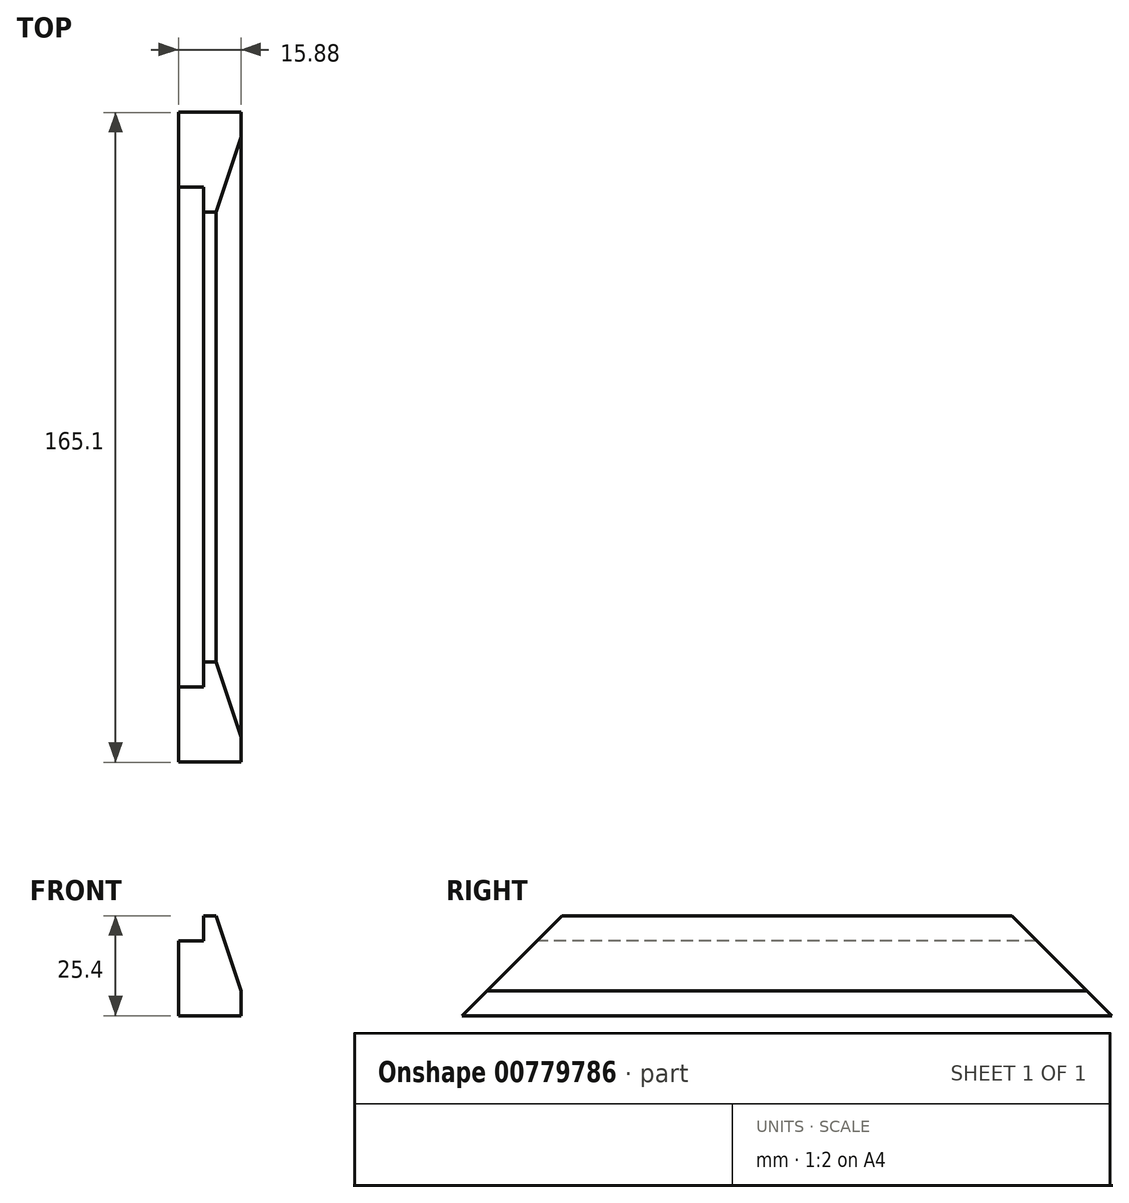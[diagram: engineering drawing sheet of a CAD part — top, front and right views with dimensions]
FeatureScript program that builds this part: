
annotation { "Feature Type Name" : "Feature", "Feature Type Description" : "" }
export const myFeature = defineFeature(function(context is Context, id is Id, definition is map)
    precondition{}
    {
        {
            var Q0;
            Q0=qCreatedBy(makeId("Right.planeOp"),FACE);
            var sketch = newSketch(context, id + "F0", { "sketchPlane" : qUnion([Q0])});
            skLineSegment(sketch, "E0.bottom", {"start": v(84.71, 12.7) * mm, "end": v(-80.39, 12.7) * mm});
            skLineSegment(sketch, "E0.top", {"start": v(84.71, -12.7) * mm, "end": v(-80.39, -12.7) * mm});
            skLineSegment(sketch, "E0.left", {"start": v(84.71, 12.7) * mm, "end": v(84.71, -12.7) * mm});
            skLineSegment(sketch, "E0.right", {"start": v(-80.39, 12.7) * mm, "end": v(-80.39, -12.7) * mm});
            skPoint(sketch, "E0.middle", {"position": v(2.16, 0) * mm});
            skSolve(sketch);
        }
        {
            var Q0;
            Q0 = qSketchRegion(id + "F0", true);
            extrude(context, id + "F1", {"entities" : qUnion([Q0]), "depth" : 15.88 * mm, "offsetDistance" : 25.4 * mm});
        }
        {
            var Q0;
            Q0=makeQuery(id+"F1.opExtrude","CAP_FACE",FACE,{"disambiguationData":[OSD([sQuery(id+"F0.wireOp",EDGE,"E0.bottom"),sQuery(id+"F0.wireOp",EDGE,"E0.top"),sQuery(id+"F0.wireOp",EDGE,"E0.left"),sQuery(id+"F0.wireOp",EDGE,"E0.right")])],"isStart":false});
            var sketch = newSketch(context, id + "F2", { "sketchPlane" : qUnion([Q0])});
            skLineSegment(sketch, "E1", {"start": v(-80.39, -12.7) * mm, "end": v(-54.99, 12.7) * mm});
            skLineSegment(sketch, "E2", {"start": v(84.71, -12.7) * mm, "end": v(59.31, 12.7) * mm});
            skSolve(sketch);
        }
        {
            var Q0;
            Q0=makeQuery(id+"F1.opExtrude","SWEPT_FACE",FACE,{"disambiguationData":[OSD([sQuery(id+"F0.wireOp",EDGE,"E0.right")])]});
            var sketch = newSketch(context, id + "F3", { "sketchPlane" : qUnion([Q0])});
            skLineSegment(sketch, "E3.bottom", {"start": v(0, 12.7) * mm, "end": v(6.35, 12.7) * mm});
            skLineSegment(sketch, "E3.top", {"start": v(0, 6.35) * mm, "end": v(6.35, 6.35) * mm});
            skLineSegment(sketch, "E3.left", {"start": v(0, 12.7) * mm, "end": v(0, 6.35) * mm});
            skLineSegment(sketch, "E3.right", {"start": v(6.35, 12.7) * mm, "end": v(6.35, 6.35) * mm});
            skSolve(sketch);
        }
        {
            var Q0;
            Q0 = qSketchRegion(id + "F3", true);
            extrude(context, id + "F4", {"entities" : qUnion([Q0]), "operationType" : NewBodyOperationType.REMOVE, "endBound" : BoundingType.THROUGH_ALL, "oppositeDirection" : true, "depth" : 25.4 * mm, "offsetDistance" : 25.4 * mm});
        }
        {
            var Q0;
            {var subQ0=sQuery(id+"F2.wireOp",EDGE,"E1");Q0=makeQuery(id+"F2.imprint","IMPRINT",FACE,{"disambiguationData":[TD([[makeQuery(id+"F2.imprint","IMPRINT",EDGE,{"derivedFrom":subQ0}),1.0]])]});}
            var Q1;
            {var subQ0=sQuery(id+"F2.wireOp",EDGE,"E2");Q1=makeQuery(id+"F2.imprint","IMPRINT",FACE,{"disambiguationData":[TD([[makeQuery(id+"F2.imprint","IMPRINT",EDGE,{"derivedFrom":subQ0}),-1.0]])]});}
            extrude(context, id + "F5", {"entities" : qUnion([Q0, Q1]), "operationType" : NewBodyOperationType.REMOVE, "endBound" : BoundingType.THROUGH_ALL, "oppositeDirection" : true, "depth" : 25.4 * mm, "offsetDistance" : 25.4 * mm});
        }
        {
            var Q0;
            Q0=makeQuery(id+"F1.opExtrude","CAP_EDGE",EDGE,{"disambiguationData":[OSD([sQuery(id+"F0.wireOp",EDGE,"E0.bottom")])],"isStart":false});
            chamfer(context, id + "F6", {"entities" : qUnion([Q0]), "chamferType" : ChamferType.OFFSET_ANGLE, "width" : 19.05 * mm, "oppositeDirection" : false, "angle" : 18.43 * degree, "tangentPropagation" : true});
        }
    });
